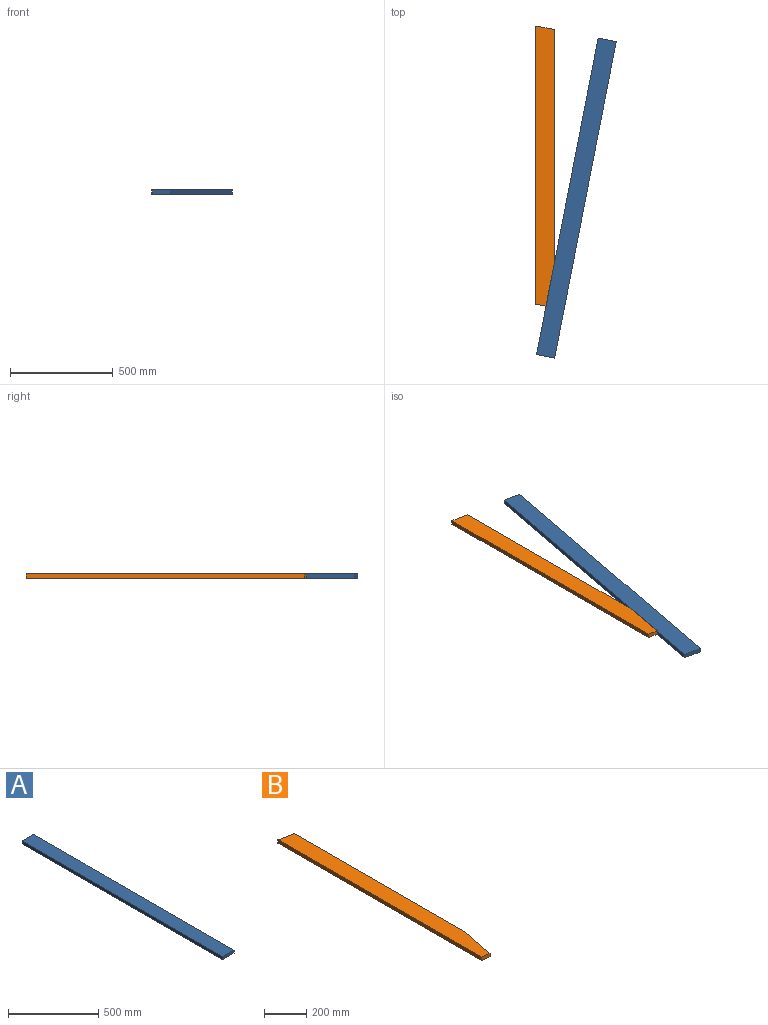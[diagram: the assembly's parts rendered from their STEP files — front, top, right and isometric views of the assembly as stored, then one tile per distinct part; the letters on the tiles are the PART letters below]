
ASSEMBLY  parts=2 mates=3
PART A: 6 faces, bbox 90x1570x20 mm
  f0: plane 1570x20mm, normal (-1,0,0), area 31400mm2, adj f1,f3,f4,f5
  f1: plane 1570x90mm, normal (0,0,-1), area 141300mm2, adj f0,f2,f4,f5
  f2: plane 1570x20mm, normal (1,0,0), area 31400mm2, adj f1,f3,f4,f5
  f3: plane 1570x90mm, normal (0,0,1), area 141300mm2, adj f0,f2,f4,f5
  f4: plane 90x20mm, normal (0,-1,0), area 1800mm2, adj f0,f1,f2,f3
  f5: plane 90x20mm, normal (0,1,0), area 1800mm2, adj f0,f1,f2,f3
PART B: 7 faces, bbox 90x1364.2x20 mm
  f0: plane 1354.5x20mm, normal (-1,0,0), area 27090mm2, adj f2,f3,f4,f6
  f1: plane 1140.94x20mm, normal (1,0,0), area 22818.8mm2, adj f2,f3,f4,f5
  f2: plane 1364.22x90mm, normal (0,0,1), area 117633.7mm2, adj f0,f1,f4,f5,f6
  f3: plane 1364.22x90mm, normal (0,0,-1), area 117633.7mm2, adj f0,f1,f4,f5,f6
  f4: plane 90x20mm, normal (0.19,0.98,0), area 1833.7mm2, adj f0,f1,f2,f3
  f5: plane 205.78x40mm, normal (0.98,-0.19,0), area 4192.7mm2, adj f1,f2,f3,f6
  f6: plane 50x20mm, normal (-0.19,-0.98,0), area 1018.7mm2, adj f0,f2,f3,f5
PLACE A rot(axis=(0,0,-1),11deg) t=(663.65,141.23,282.12)mm fixed
PLACE B rot(axis=(0,0,1),0deg) t=(359.95,200.27,282.12)mm
MATE planar A.f5 <-> B.f4  axis (0.19,0.98,0) through (707.83,132.65,292.12)mm
MATE planar A.f0 <-> B.f5  axis (-0.98,0.19,0) through (513.87,-629.35,292.12)mm
MATE planar A.f3 <-> B.f2  axis (0,0,1) through (558.04,-637.93,302.12)mm
